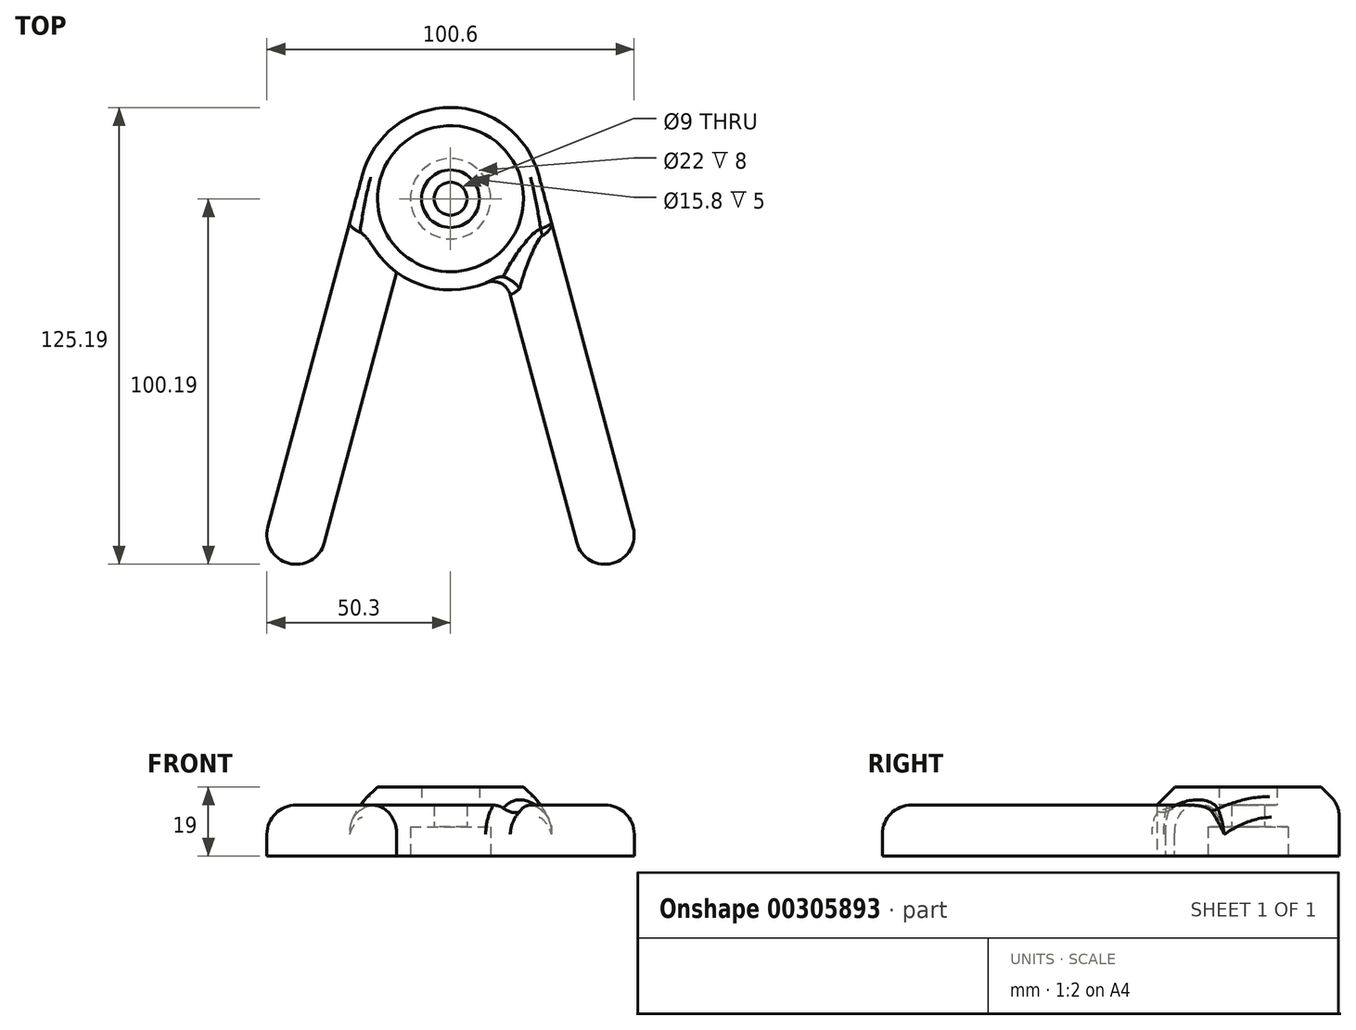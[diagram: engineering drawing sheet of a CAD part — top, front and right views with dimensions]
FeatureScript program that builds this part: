
annotation { "Feature Type Name" : "Feature", "Feature Type Description" : "" }
export const myFeature = defineFeature(function(context is Context, id is Id, definition is map)
    precondition{}
    {
        {
            var Q0;
            Q0=qCreatedBy(makeId("Top.planeOp"),FACE);
            var sketch = newSketch(context, id + "F0", { "sketchPlane" : qUnion([Q0])});
            skLineSegment(sketch, "E0", {"start": v(24.15, 6.47) * mm, "end": v(50.03, -90.12) * mm});
            skLineSegment(sketch, "E1", {"start": v(34.58, -94.26) * mm, "end": v(14.73, -20.2) * mm});
            skArc(sketch, "E2", {"start": v(24.15, 6.47) * mm, "mid": v(15.22, 19.83) * mm, "end": v(0, 25) * mm});
            skArc(sketch, "E3", {"start": v(0, -25) * mm, "mid": v(7.75, -23.77) * mm, "end": v(14.73, -20.2) * mm});
            skArc(sketch, "E4", {"start": v(0, -4.5) * mm, "mid": v(4.5, 0) * mm, "end": v(0, 4.5) * mm});
            skArc(sketch, "E5", {"start": v(50.03, -90.12) * mm, "mid": v(44.37, -99.92) * mm, "end": v(34.58, -94.26) * mm});
            skLineSegment(sketch, "E6.MirrorCS", {"start": v(-24.15, 6.47) * mm, "end": v(-50.03, -90.12) * mm});
            skArc(sketch, "E7.MirrorCS", {"start": v(0, -4.5) * mm, "mid": v(-4.5, 0) * mm, "end": v(0, 4.5) * mm});
            skArc(sketch, "E8.MirrorCS", {"start": v(-50.03, -90.12) * mm, "mid": v(-44.37, -99.92) * mm, "end": v(-34.58, -94.26) * mm});
            skLineSegment(sketch, "E9.MirrorCS", {"start": v(-34.58, -94.26) * mm, "end": v(-14.73, -20.2) * mm});
            skArc(sketch, "E10.MirrorCS", {"start": v(-24.15, 6.47) * mm, "mid": v(-15.22, 19.83) * mm, "end": v(0, 25) * mm});
            skArc(sketch, "E11.MirrorCS", {"start": v(0, -25) * mm, "mid": v(-7.75, -23.77) * mm, "end": v(-14.73, -20.2) * mm});
            skSolve(sketch);
        }
        {
            var Q0;
            Q0=makeQuery(id+"F0.imprint","IMPRINT",FACE,{"disambiguationData":[TD([[makeQuery(id+"F0.imprint","IMPRINT",EDGE,{"derivedFrom":sQuery(id+"F0.wireOp",EDGE,"E0")}),-1.0]])]});
            extrude(context, id + "F1", {"entities" : qUnion([Q0]), "depth" : 14 * mm});
        }
        {
            var Q0;
            Q0=makeQuery(id+"F1.opExtrude","CAP_FACE",FACE,{"disambiguationData":[OSD([sQuery(id+"F0.wireOp",EDGE,"E0"),sQuery(id+"F0.wireOp",EDGE,"E1"),sQuery(id+"F0.wireOp",EDGE,"E2"),sQuery(id+"F0.wireOp",EDGE,"E3"),sQuery(id+"F0.wireOp",EDGE,"E4"),sQuery(id+"F0.wireOp",EDGE,"E5"),sQuery(id+"F0.wireOp",EDGE,"E6.MirrorCS"),sQuery(id+"F0.wireOp",EDGE,"E7.MirrorCS"),sQuery(id+"F0.wireOp",EDGE,"E8.MirrorCS"),sQuery(id+"F0.wireOp",EDGE,"E9.MirrorCS"),sQuery(id+"F0.wireOp",EDGE,"E10.MirrorCS"),sQuery(id+"F0.wireOp",EDGE,"E11.MirrorCS")])],"isStart":true});
            var sketch = newSketch(context, id + "F2", { "sketchPlane" : qUnion([Q0])});
            skCircle(sketch, "E12", {"center": v(0, 0) * mm, "radius": 11 * mm});
            skSolve(sketch);
        }
        {
            var Q0;
            Q0=makeQuery(id+"F2.imprint","IMPRINT",FACE,{"disambiguationData":[TD([[makeQuery(id+"F2.imprint","IMPRINT",EDGE,{"derivedFrom":sQuery(id+"F2.wireOp",EDGE,"E12")}),1.0]])]});
            extrude(context, id + "F3", {"entities" : qUnion([Q0]), "operationType" : NewBodyOperationType.REMOVE, "oppositeDirection" : true, "depth" : 8 * mm});
        }
        {
            var Q0;
            Q0=makeQuery(id+"F1.opExtrude","CAP_FACE",FACE,{"disambiguationData":[OSD([sQuery(id+"F0.wireOp",EDGE,"E0"),sQuery(id+"F0.wireOp",EDGE,"E1"),sQuery(id+"F0.wireOp",EDGE,"E2"),sQuery(id+"F0.wireOp",EDGE,"E3"),sQuery(id+"F0.wireOp",EDGE,"E4"),sQuery(id+"F0.wireOp",EDGE,"E5"),sQuery(id+"F0.wireOp",EDGE,"E6.MirrorCS"),sQuery(id+"F0.wireOp",EDGE,"E7.MirrorCS"),sQuery(id+"F0.wireOp",EDGE,"E8.MirrorCS"),sQuery(id+"F0.wireOp",EDGE,"E9.MirrorCS"),sQuery(id+"F0.wireOp",EDGE,"E10.MirrorCS"),sQuery(id+"F0.wireOp",EDGE,"E11.MirrorCS")])],"isStart":false});
            var sketch = newSketch(context, id + "F4", { "sketchPlane" : qUnion([Q0])});
            skCircle(sketch, "E13", {"center": v(0, 0) * mm, "radius": 25 * mm});
            skCircle(sketch, "E14", {"center": v(0, 0) * mm, "radius": 7.9 * mm});
            skSolve(sketch);
        }
        {
            var Q0;
            Q0=makeQuery(id+"F4.imprint","IMPRINT",FACE,{"disambiguationData":[TD([[makeQuery(id+"F4.imprint","IMPRINT",EDGE,{"derivedFrom":sQuery(id+"F4.wireOp",EDGE,"E14")}),-1.0]])]});
            extrude(context, id + "F5", {"entities" : qUnion([Q0]), "operationType" : NewBodyOperationType.ADD, "depth" : 5 * mm});
        }
        {
            var Q0;
            Q0=makeQuery(id+"F5.opExtrude","CAP_EDGE",EDGE,{"disambiguationData":[OSD([sQuery(id+"F4.wireOp",EDGE,"E13")])],"isStart":false});
            chamfer(context, id + "F6", {"entities" : qUnion([Q0]), "width" : 5 * mm, "tangentPropagation" : true});
        }
        {
            var Q0;
            Q0=makeQuery(id+"F1.opExtrude","CAP_EDGE",EDGE,{"disambiguationData":[OSD([sQuery(id+"F0.wireOp",EDGE,"E8.MirrorCS")])],"isStart":false});
            var Q1;
            Q1=makeQuery(id+"F1.opExtrude","CAP_EDGE",EDGE,{"disambiguationData":[OSD([sQuery(id+"F0.wireOp",EDGE,"E1")])],"isStart":false});
            fillet(context, id + "F7", {"entities" : qUnion([Q0, Q1]), "radius" : 8 * mm, "tangentPropagation" : true, "allowEdgeOverflow" : false});
        }
        {
            var Q0;
            Q0=makeQuery(id+"F7.opFillet","BLEND_EDGE",EDGE,{"blendedFrom":[makeQuery(id+"F1.opExtrude","CAP_EDGE",EDGE,{"disambiguationData":[OSD([sQuery(id+"F0.wireOp",EDGE,"E6.MirrorCS")])],"isStart":false}),makeQuery(id+"F6.opChamfer","SPLIT",FACE,{"disambiguationData":[OD(0.0)],"derivedFrom":makeQuery(id+"F5.boolean.opBoolean","MERGE",FACE,{"derivedFrom":[makeQuery(id+"F1.opExtrude","SWEPT_FACE",FACE,{"disambiguationData":[OSD([sQuery(id+"F0.wireOp",EDGE,"E2"),sQuery(id+"F0.wireOp",EDGE,"E10.MirrorCS")])]}),makeQuery(id+"F1.opExtrude","SWEPT_FACE",FACE,{"disambiguationData":[OSD([sQuery(id+"F0.wireOp",EDGE,"E3"),sQuery(id+"F0.wireOp",EDGE,"E11.MirrorCS")])]}),makeQuery(id+"F5.opExtrude","SWEPT_FACE",FACE,{"disambiguationData":[OSD([sQuery(id+"F4.wireOp",EDGE,"E13")])]})]})})],"blendedInto":[makeQuery(id+"F6.opChamfer","SPLIT",FACE,{"disambiguationData":[OD(0.0)],"derivedFrom":makeQuery(id+"F5.boolean.opBoolean","MERGE",FACE,{"derivedFrom":[makeQuery(id+"F1.opExtrude","SWEPT_FACE",FACE,{"disambiguationData":[OSD([sQuery(id+"F0.wireOp",EDGE,"E2"),sQuery(id+"F0.wireOp",EDGE,"E10.MirrorCS")])]}),makeQuery(id+"F1.opExtrude","SWEPT_FACE",FACE,{"disambiguationData":[OSD([sQuery(id+"F0.wireOp",EDGE,"E3"),sQuery(id+"F0.wireOp",EDGE,"E11.MirrorCS")])]}),makeQuery(id+"F5.opExtrude","SWEPT_FACE",FACE,{"disambiguationData":[OSD([sQuery(id+"F4.wireOp",EDGE,"E13")])]})]})})]});
            var Q1;
            Q1=makeQuery(id+"F1.opExtrude","SWEPT_EDGE",EDGE,{"disambiguationData":[OSD([sQuery(id+"F0.wireOp",EDGE,"E1"),sQuery(id+"F0.wireOp",EDGE,"E3")])]});
            fillet(context, id + "F8", {"entities" : qUnion([Q0, Q1]), "radius" : 5 * mm, "tangentPropagation" : true, "allowEdgeOverflow" : false});
        }
    });
